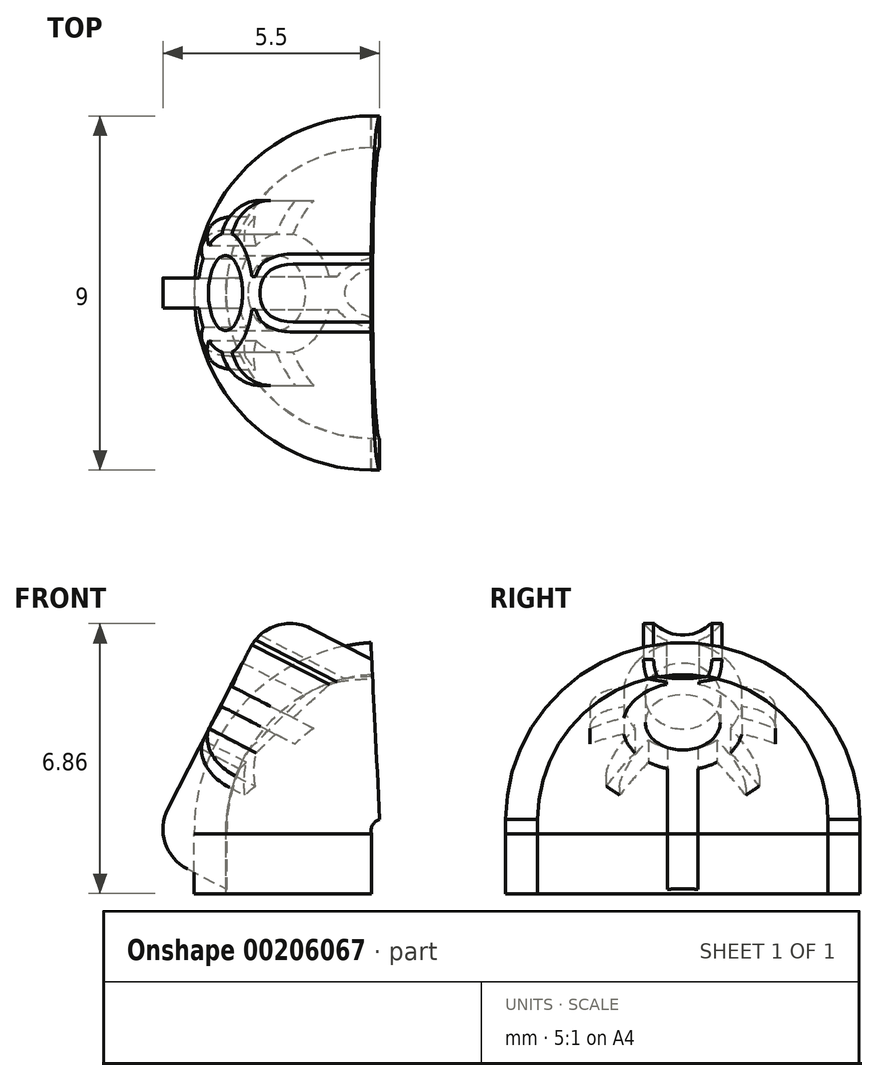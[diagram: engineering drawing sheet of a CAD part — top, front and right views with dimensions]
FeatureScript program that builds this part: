
annotation { "Feature Type Name" : "Feature", "Feature Type Description" : "" }
export const myFeature = defineFeature(function(context is Context, id is Id, definition is map)
    precondition{}
    {
        {
            var Q0;
            Q0=qCreatedBy(makeId("Top.planeOp"),FACE);
            var sketch = newSketch(context, id + "F0", { "sketchPlane" : qUnion([Q0])});
            skLineSegment(sketch, "E0", {"start": v(0, -0.75) * mm, "end": v(0, -0.62) * mm});
            skArc(sketch, "E1", {"start": v(0, 0.75) * mm, "mid": v(-0.75, 0) * mm, "end": v(0, -0.75) * mm});
            skArc(sketch, "E2.0", {"start": v(0, 0.62) * mm, "mid": v(-0.62, 0) * mm, "end": v(0, -0.62) * mm});
            skLineSegment(sketch, "E3.trimOffspring", {"start": v(0, 0.62) * mm, "end": v(0, 0.75) * mm});
            skSolve(sketch);
        }
        {
            var Q0;
            Q0=qCreatedBy(makeId("Front.planeOp"),FACE);
            var sketch = newSketch(context, id + "F1", { "sketchPlane" : qUnion([Q0])});
            skArc(sketch, "E4", {"start": v(0, 0.76) * mm, "mid": v(-0.5, 0.52) * mm, "end": v(-0.7, 0) * mm});
            skSolve(sketch);
        }
        {
            var Q0;
            Q0=qSketchRegion(id+"F0",true);
            var Q1;
            Q1=qConstructionFilter(qBodyType(qCreatedBy(id+"F0",EDGE),BodyType.WIRE),ConstructionObject.NO);
            var Q2;
            Q2=qConstructionFilter(qBodyType(qCreatedBy(id+"F1",EDGE),BodyType.WIRE),ConstructionObject.NO);
            sweep(context, id + "F2", {"profiles" : qUnion([Q0]), "surfaceProfiles" : qUnion([Q1]), "path" : qUnion([Q2])});
        }
        {
            var Q0;
            Q0=makeQuery(id+"F2.opSweep","SWEPT_BODY",BODY,{"disambiguationData":[OSD([sQuery(id+"F0.wireOp",EDGE,"E0"),sQuery(id+"F0.wireOp",EDGE,"E1"),sQuery(id+"F0.wireOp",EDGE,"E2.0"),sQuery(id+"F0.wireOp",EDGE,"E3.trimOffspring"),sQuery(id+"F1.wireOp",EDGE,"E4")])]});
            var Q1;
            Q1=makeQuery(id+"FvTfHQbpZwPaBW4_1.opExtrude","SWEPT_BODY",BODY,{"disambiguationData":[OSD([sQuery(id+"FDmz0f5WjvM4FEd_1.wireOp",EDGE,"2DNLliUg-4gvH-zFux-c9ot-hAgfZaulDJ3o"),sQuery(id+"FDmz0f5WjvM4FEd_1.wireOp",EDGE,"LoKV8Df2-YKVr-Pj7b-xbhj-xFJiWo8RZIE2"),sQuery(id+"FDmz0f5WjvM4FEd_1.wireOp",EDGE,"RDnQLvbl-YGKO-oPLK-rJ1k-2vc6lgI1f4HU"),sQuery(id+"FDmz0f5WjvM4FEd_1.wireOp",EDGE,"R8v6pF6o-81fq-Mgd0-Zibu-v6kVc1jocJu6"),sQuery(id+"FDmz0f5WjvM4FEd_1.wireOp",EDGE,"tyPqoxrv-9rbv-4UdE-hqcg-FmuSsGJ96tp6"),sQuery(id+"FDmz0f5WjvM4FEd_1.wireOp",EDGE,"H6YguFUV-EZgk-eS7r-mbRd-MBfkXEixhvqo"),sQuery(id+"FDmz0f5WjvM4FEd_1.wireOp",EDGE,"MNr5xkYj-95uR-RlIY-UyhE-asRXDi0gZT7A"),sQuery(id+"FDmz0f5WjvM4FEd_1.wireOp",EDGE,"toU3CRjA-NfvW-irf8-ibOq-aOgjNhvAM4kX"),sQuery(id+"FDmz0f5WjvM4FEd_1.wireOp",EDGE,"0fEWQNN0-lG67-jiUm-4nkk-8WpPiNwknb3L"),sQuery(id+"FDmz0f5WjvM4FEd_1.wireOp",EDGE,"aeb0d396-f790-42ac-a34d-5cb2a2e761f00.MirrorCS"),sQuery(id+"FDmz0f5WjvM4FEd_1.wireOp",EDGE,"0ov03eKC-B9wZ-xMWz-a2vB-RilsfYAVgbFf"),sQuery(id+"FDmz0f5WjvM4FEd_1.wireOp",EDGE,"4d2b5762-7691-463b-b7ab-f9b2dd690ff4.trimOffspring"),sQuery(id+"FDmz0f5WjvM4FEd_1.wireOp",EDGE,"d9c17598-795f-4659-85ec-610b1b5948a20.MirrorCS"),sQuery(id+"FDmz0f5WjvM4FEd_1.wireOp",EDGE,"d72de5a5-37b5-4cc8-98f5-1ff9a8c2d66e0.MirrorCS"),sQuery(id+"FDmz0f5WjvM4FEd_1.wireOp",EDGE,"286a638d-49f9-4aec-8dad-e7d0139cea390.MirrorCS"),sQuery(id+"FDmz0f5WjvM4FEd_1.wireOp",EDGE,"071fcbf1-2387-4bfd-858f-0bf6015ef5d80.MirrorCS"),sQuery(id+"FDmz0f5WjvM4FEd_1.wireOp",EDGE,"90ee7c01-a75b-498b-b861-7f5bc27a31380.MirrorCS"),sQuery(id+"FDmz0f5WjvM4FEd_1.wireOp",EDGE,"17709a1d-5500-4bf7-9508-dd0255d6a65d0.MirrorCS"),sQuery(id+"FDmz0f5WjvM4FEd_1.wireOp",EDGE,"e4f1f56c-616a-4b60-bc45-ff655f755af00.MirrorCS"),sQuery(id+"FDmz0f5WjvM4FEd_1.wireOp",EDGE,"cd95b208-d1fe-4f11-862d-512c6186efd80.MirrorCS"),sQuery(id+"FDmz0f5WjvM4FEd_1.wireOp",EDGE,"b36ab7d9-dd3d-4c50-8c93-ce816075e1fe0.MirrorCS"),sQuery(id+"FDmz0f5WjvM4FEd_1.wireOp",EDGE,"cefc95d8-cf7d-4c8d-9a61-ceb47b642b96.trimOffspring"),sQuery(id+"FDmz0f5WjvM4FEd_1.wireOp",EDGE,"129a8ffe-56ec-4a78-9746-da5512898f1b.trimOffspring"),sQuery(id+"FDmz0f5WjvM4FEd_1.wireOp",EDGE,"d6bb9b85-002c-4b73-91bd-9782b8dc5f5a.trimOffspring")])]});
            var Q2;
            Q2=makeQuery(id+"FvTfHQbpZwPaBW4_1.opExtrude","SWEPT_BODY",BODY,{"disambiguationData":[OSD([sQuery(id+"FDmz0f5WjvM4FEd_1.wireOp",EDGE,"uPfLpDPh-7yLI-ApWV-yZhU-S8zxpAj9hg6U"),sQuery(id+"FDmz0f5WjvM4FEd_1.wireOp",EDGE,"fMEL1x15-G0ZE-0lUB-CcH6-RP9cVj1G8mGl"),sQuery(id+"FDmz0f5WjvM4FEd_1.wireOp",EDGE,"fazZkoOm-3IBO-zVTZ-vRJ6-EP1tbFfi50OC"),sQuery(id+"FDmz0f5WjvM4FEd_1.wireOp",EDGE,"d4930700-33d1-4082-b912-5a05ab66b6a8.trimOffspring")])]});
            var Q3;
            Q3=sQuery(id+"F0.wireOp",EDGE,"E0");
            var Q4;
            Q4=sQuery(id+"F0.wireOp",VERTEX,"E2.0.center");
            transform(context, id + "F3", {"entities" : qUnion([Q0, Q1, Q2]), "transformType" : TransformType.SCALE_UNIFORMLY, "scale" : 6, "scalePoint" : qUnion([Q4]), "makeCopy" : false});
        }
        {
            var Q0;
            Q0=makeQuery(id+"F2.opSweep","CAP_FACE",FACE,{"disambiguationData":[OSD([sQuery(id+"F0.wireOp",EDGE,"E0"),sQuery(id+"F0.wireOp",EDGE,"E1"),sQuery(id+"F0.wireOp",EDGE,"E2.0"),sQuery(id+"F0.wireOp",EDGE,"E3.trimOffspring"),sQuery(id+"F1.wireOp",VERTEX,"E4.end")])],"isStart":true});
            var sketch = newSketch(context, id + "F4", { "sketchPlane" : qUnion([Q0])});
            skArc(sketch, "E5", {"start": v(0, 4.5) * mm, "mid": v(-4.5, 0) * mm, "end": v(0, -4.5) * mm});
            skArc(sketch, "E6", {"start": v(0, 3.7) * mm, "mid": v(-3.7, 0) * mm, "end": v(0, -3.7) * mm});
            skLineSegment(sketch, "E7", {"start": v(0, 4.5) * mm, "end": v(0, 3.7) * mm});
            skLineSegment(sketch, "E8", {"start": v(0, -3.7) * mm, "end": v(0, -4.5) * mm});
            skSolve(sketch);
        }
        {
            var Q0;
            Q0 = qSketchRegion(id + "F4", true);
            extrude(context, id + "F5", {"entities" : qUnion([Q0]), "operationType" : NewBodyOperationType.ADD, "depth" : 1.52 * mm});
        }
        {
            var Q0;
            Q0=makeQuery(id+"F2.opSweep","CAP_FACE",FACE,{"disambiguationData":[OSD([sQuery(id+"F0.wireOp",EDGE,"E0"),sQuery(id+"F0.wireOp",EDGE,"E1"),sQuery(id+"F0.wireOp",EDGE,"E2.0"),sQuery(id+"F0.wireOp",EDGE,"E3.trimOffspring"),sQuery(id+"F1.wireOp",VERTEX,"E4.start")])],"isStart":false});
            var Q1;
            Q1=makeQuery(id+"F5.opExtrude","CAP_EDGE",EDGE,{"disambiguationData":[OSD([sQuery(id+"F4.wireOp",EDGE,"E7")])],"isStart":false});
            cPlane(context, id + "F6", {"entities" : qUnion([Q0, Q1]), "cplaneType" : CPlaneType.LINE_ANGLE, "offset" : 25.4 * mm, "angle" : 30 * degree, "width" : 152.4 * mm, "height" : 152.4 * mm});
        }
        {
            var Q0;
            Q0=qCreatedBy(id+"F6.planeOp",FACE);
            var sketch = newSketch(context, id + "F7", { "sketchPlane" : qUnion([Q0])});
            skCircle(sketch, "E9", {"center": v(0, 1.42) * mm, "radius": 0.95 * mm});
            skArc(sketch, "E10", {"start": v(-0.42, 2.89) * mm, "mid": v(-1.12, 2.46) * mm, "end": v(-1.5, 1.72) * mm});
            skArc(sketch, "E11", {"start": v(-1, 3.94) * mm, "mid": v(-0.84, 3.4) * mm, "end": v(-0.42, 3.04) * mm});
            skArc(sketch, "E12", {"start": v(-0.74, 3.94) * mm, "mid": v(0, 3.2) * mm, "end": v(0.74, 3.94) * mm});
            skLineSegment(sketch, "E13", {"start": v(1, 3.94) * mm, "end": v(0.74, 3.94) * mm});
            skLineSegment(sketch, "E14.trimOffspring", {"start": v(-0.74, 3.94) * mm, "end": v(-1, 3.94) * mm});
            skLineSegment(sketch, "E15", {"start": v(-0.42, 3.04) * mm, "end": v(-0.42, 2.89) * mm});
            skLineSegment(sketch, "E16", {"start": v(0, -3.34) * mm, "end": v(-0.38, -3.34) * mm});
            skLineSegment(sketch, "E17", {"start": v(-0.38, -2.93) * mm, "end": v(-0.38, -0.05) * mm});
            skLineSegment(sketch, "E18", {"start": v(-1.94, -0.27) * mm, "end": v(-1.21, 0.5) * mm});
            skLineSegment(sketch, "E19.MirrorCS", {"start": v(-1.6, -0.6) * mm, "end": v(-0.87, 0.17) * mm});
            skLineSegment(sketch, "E20", {"start": v(-1.6, -0.6) * mm, "end": v(-1.94, -0.27) * mm});
            skLineSegment(sketch, "E21.MirrorCS", {"start": v(0.38, -2.93) * mm, "end": v(0.38, -0.05) * mm});
            skLineSegment(sketch, "E22.MirrorCS", {"start": v(1.6, -0.6) * mm, "end": v(0.87, 0.17) * mm});
            skLineSegment(sketch, "E23.MirrorCS", {"start": v(1.6, -0.6) * mm, "end": v(1.94, -0.27) * mm});
            skLineSegment(sketch, "E24.MirrorCS", {"start": v(1.94, -0.27) * mm, "end": v(1.21, 0.5) * mm});
            skLineSegment(sketch, "E25.MirrorCS", {"start": v(2.35, 1.42) * mm, "end": v(2.35, 1.15) * mm});
            skLineSegment(sketch, "E26.MirrorCS", {"start": v(2.35, 1.42) * mm, "end": v(2.35, 1.72) * mm});
            skLineSegment(sketch, "E27.MirrorCS", {"start": v(0.42, 3.04) * mm, "end": v(0.42, 2.89) * mm});
            skArc(sketch, "E28.trimOffspring", {"start": v(0.42, 3.04) * mm, "mid": v(0.84, 3.4) * mm, "end": v(1, 3.94) * mm});
            skArc(sketch, "E29.trimOffspring", {"start": v(-1.5, 1.15) * mm, "mid": v(-1.4, 0.8) * mm, "end": v(-1.21, 0.5) * mm});
            skArc(sketch, "E30.trimOffspring", {"start": v(-0.87, 0.17) * mm, "mid": v(-0.64, 0.04) * mm, "end": v(-0.38, -0.05) * mm});
            skArc(sketch, "E31.trimOffspring", {"start": v(0.38, -0.05) * mm, "mid": v(0.64, 0.04) * mm, "end": v(0.87, 0.17) * mm});
            skArc(sketch, "E32.trimOffspring", {"start": v(1.21, 0.5) * mm, "mid": v(1.4, 0.8) * mm, "end": v(1.5, 1.15) * mm});
            skArc(sketch, "E33.trimOffspring", {"start": v(1.47, 1.82) * mm, "mid": v(1.08, 2.5) * mm, "end": v(0.42, 2.89) * mm});
            skLineSegment(sketch, "E34", {"start": v(-0.38, -2.93) * mm, "end": v(0.38, -2.93) * mm});
            skLineSegment(sketch, "E35", {"start": v(2.35, 1.72) * mm, "end": v(1.5, 1.72) * mm});
            skLineSegment(sketch, "E36", {"start": v(2.35, 1.15) * mm, "end": v(1.5, 1.15) * mm});
            skArc(sketch, "E37.trimOffspring", {"start": v(1.5, 1.72) * mm, "mid": v(1.48, 1.77) * mm, "end": v(1.47, 1.82) * mm});
            skLineSegment(sketch, "E38.MirrorCS", {"start": v(-2.35, 1.15) * mm, "end": v(-1.5, 1.15) * mm});
            skLineSegment(sketch, "E39.MirrorCS", {"start": v(-2.35, 1.42) * mm, "end": v(-2.35, 1.15) * mm});
            skLineSegment(sketch, "E40.MirrorCS", {"start": v(-2.35, 1.42) * mm, "end": v(-2.35, 1.72) * mm});
            skLineSegment(sketch, "E41.MirrorCS", {"start": v(-2.35, 1.72) * mm, "end": v(-1.5, 1.72) * mm});
            skSolve(sketch);
        }
        {
            var Q0;
            Q0 = qSketchRegion(id + "F7", true);
            extrude(context, id + "F8", {"entities" : qUnion([Q0]), "depth" : 5.6 * mm});
        }
        {
            var Q0;
            Q0=makeQuery(id+"F8.opExtrude","CAP_FACE",FACE,{"disambiguationData":[OSD([sQuery(id+"F7.wireOp",EDGE,"E9"),sQuery(id+"F7.wireOp",EDGE,"E10"),sQuery(id+"F7.wireOp",EDGE,"E11"),sQuery(id+"F7.wireOp",EDGE,"E12"),sQuery(id+"F7.wireOp",EDGE,"E13"),sQuery(id+"F7.wireOp",EDGE,"E14.trimOffspring"),sQuery(id+"F7.wireOp",EDGE,"E15"),sQuery(id+"F7.wireOp",EDGE,"E17"),sQuery(id+"F7.wireOp",EDGE,"E18"),sQuery(id+"F7.wireOp",EDGE,"E19.MirrorCS"),sQuery(id+"F7.wireOp",EDGE,"E20"),sQuery(id+"F7.wireOp",EDGE,"E21.MirrorCS"),sQuery(id+"F7.wireOp",EDGE,"E22.MirrorCS"),sQuery(id+"F7.wireOp",EDGE,"E23.MirrorCS"),sQuery(id+"F7.wireOp",EDGE,"E24.MirrorCS"),sQuery(id+"F7.wireOp",EDGE,"E25.MirrorCS"),sQuery(id+"F7.wireOp",EDGE,"E26.MirrorCS"),sQuery(id+"F7.wireOp",EDGE,"E27.MirrorCS"),sQuery(id+"F7.wireOp",EDGE,"E28.trimOffspring"),sQuery(id+"F7.wireOp",EDGE,"E29.trimOffspring"),sQuery(id+"F7.wireOp",EDGE,"E30.trimOffspring"),sQuery(id+"F7.wireOp",EDGE,"E31.trimOffspring"),sQuery(id+"F7.wireOp",EDGE,"E32.trimOffspring"),sQuery(id+"F7.wireOp",EDGE,"E33.trimOffspring"),sQuery(id+"F7.wireOp",EDGE,"E34"),sQuery(id+"F7.wireOp",EDGE,"E35"),sQuery(id+"F7.wireOp",EDGE,"E36"),sQuery(id+"F7.wireOp",EDGE,"E37.trimOffspring"),sQuery(id+"F7.wireOp",EDGE,"E38.MirrorCS"),sQuery(id+"F7.wireOp",EDGE,"E39.MirrorCS"),sQuery(id+"F7.wireOp",EDGE,"E40.MirrorCS"),sQuery(id+"F7.wireOp",EDGE,"E41.MirrorCS")])],"isStart":true});
            var Q1;
            Q1=makeQuery(id+"F2.opSweep","SWEPT_BODY",BODY,{"disambiguationData":[OSD([sQuery(id+"F0.wireOp",EDGE,"E0"),sQuery(id+"F0.wireOp",EDGE,"E1"),sQuery(id+"F0.wireOp",EDGE,"E2.0"),sQuery(id+"F0.wireOp",EDGE,"E3.trimOffspring"),sQuery(id+"F1.wireOp",EDGE,"E4")])]});
            extrude(context, id + "F9", {"entities" : qUnion([Q0]), "operationType" : NewBodyOperationType.REMOVE, "endBound" : BoundingType.UP_TO_BODY, "oppositeDirection" : true, "endBoundEntityBody" : qUnion([Q1]), "depth" : 25.4 * mm});
        }
        {
            var Q0;
            Q0=makeQuery(id+"F8.opExtrude","CAP_EDGE",EDGE,{"disambiguationData":[OSD([sQuery(id+"F7.wireOp",EDGE,"E34")])],"isStart":false});
            var Q1;
            Q1=makeQuery(id+"F8.opExtrude","CAP_EDGE",EDGE,{"disambiguationData":[OSD([sQuery(id+"F7.wireOp",EDGE,"E25.MirrorCS"),sQuery(id+"F7.wireOp",EDGE,"E26.MirrorCS")])],"isStart":false});
            var Q2;
            Q2=makeQuery(id+"F8.opExtrude","CAP_EDGE",EDGE,{"disambiguationData":[OSD([sQuery(id+"F7.wireOp",EDGE,"E23.MirrorCS")])],"isStart":false});
            var Q3;
            Q3=makeQuery(id+"F8.opExtrude","CAP_EDGE",EDGE,{"disambiguationData":[OSD([sQuery(id+"F7.wireOp",EDGE,"E20")])],"isStart":false});
            var Q4;
            Q4=makeQuery(id+"F8.opExtrude","CAP_EDGE",EDGE,{"disambiguationData":[OSD([sQuery(id+"F7.wireOp",EDGE,"E39.MirrorCS"),sQuery(id+"F7.wireOp",EDGE,"E40.MirrorCS")])],"isStart":false});
            var Q5;
            Q5=makeQuery(id+"F8.opExtrude","CAP_EDGE",EDGE,{"disambiguationData":[OSD([sQuery(id+"F7.wireOp",EDGE,"E14.trimOffspring")])],"isStart":false});
            var Q6;
            Q6=makeQuery(id+"F8.opExtrude","CAP_EDGE",EDGE,{"disambiguationData":[OSD([sQuery(id+"F7.wireOp",EDGE,"E13")])],"isStart":false});
            fillet(context, id + "F10", {"entities" : qUnion([Q0, Q1, Q2, Q3, Q4, Q5, Q6]), "radius" : 1.14 * mm, "tangentPropagation" : true, "allowEdgeOverflow" : false});
        }
    });
